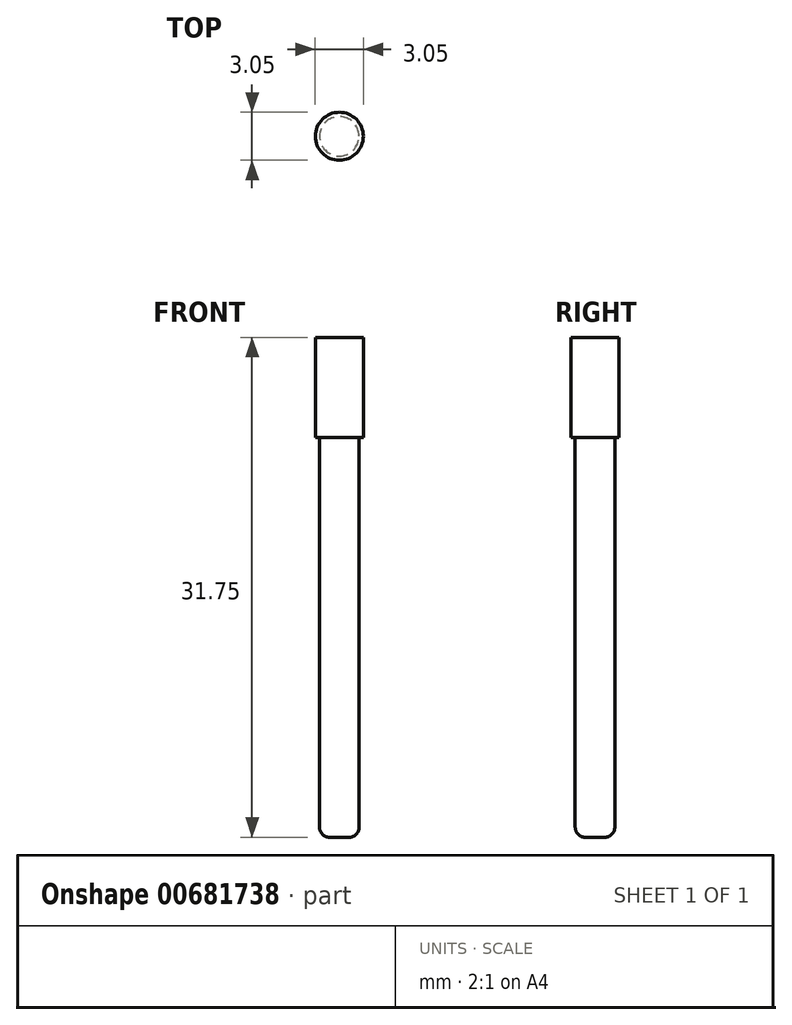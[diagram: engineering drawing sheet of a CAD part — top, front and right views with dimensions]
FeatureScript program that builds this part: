
annotation { "Feature Type Name" : "Feature", "Feature Type Description" : "" }
export const myFeature = defineFeature(function(context is Context, id is Id, definition is map)
    precondition{}
    {
        {
            var Q0;
            Q0=qCreatedBy(makeId("Top.planeOp"),FACE);
            var sketch = newSketch(context, id + "F0", { "sketchPlane" : qUnion([Q0])});
            skCircle(sketch, "E0", {"center": v(-16.26, 27.2) * mm, "radius": 1.52 * mm});
            skSolve(sketch);
        }
        {
            var Q0;
            Q0 = qSketchRegion(id + "F0", true);
            extrude(context, id + "F1", {"entities" : qUnion([Q0]), "depth" : 6.35 * mm, "offsetDistance" : 25.4 * mm});
        }
        {
            var Q0;
            Q0=makeQuery(id+"F1.opExtrude","CAP_FACE",FACE,{"disambiguationData":[OSD([sQuery(id+"F0.wireOp",EDGE,"E0")])],"isStart":true});
            var sketch = newSketch(context, id + "F2", { "sketchPlane" : qUnion([Q0])});
            skCircle(sketch, "E1", {"center": v(-16.26, -27.2) * mm, "radius": 1.26 * mm});
            skSolve(sketch);
        }
        {
            var Q0;
            Q0 = qSketchRegion(id + "F2", true);
            extrude(context, id + "F3", {"entities" : qUnion([Q0]), "operationType" : NewBodyOperationType.ADD, "depth" : 25.4 * mm, "offsetDistance" : 25.4 * mm});
        }
        {
            var Q0;
            Q0=makeQuery(id+"F3.opExtrude","CAP_EDGE",EDGE,{"disambiguationData":[OSD([sQuery(id+"F2.wireOp",EDGE,"E1")])],"isStart":false});
            fillet(context, id + "F4", {"entities" : qUnion([Q0]), "radius" : 0.64 * mm, "tangentPropagation" : true, "allowEdgeOverflow" : false});
        }
    });
